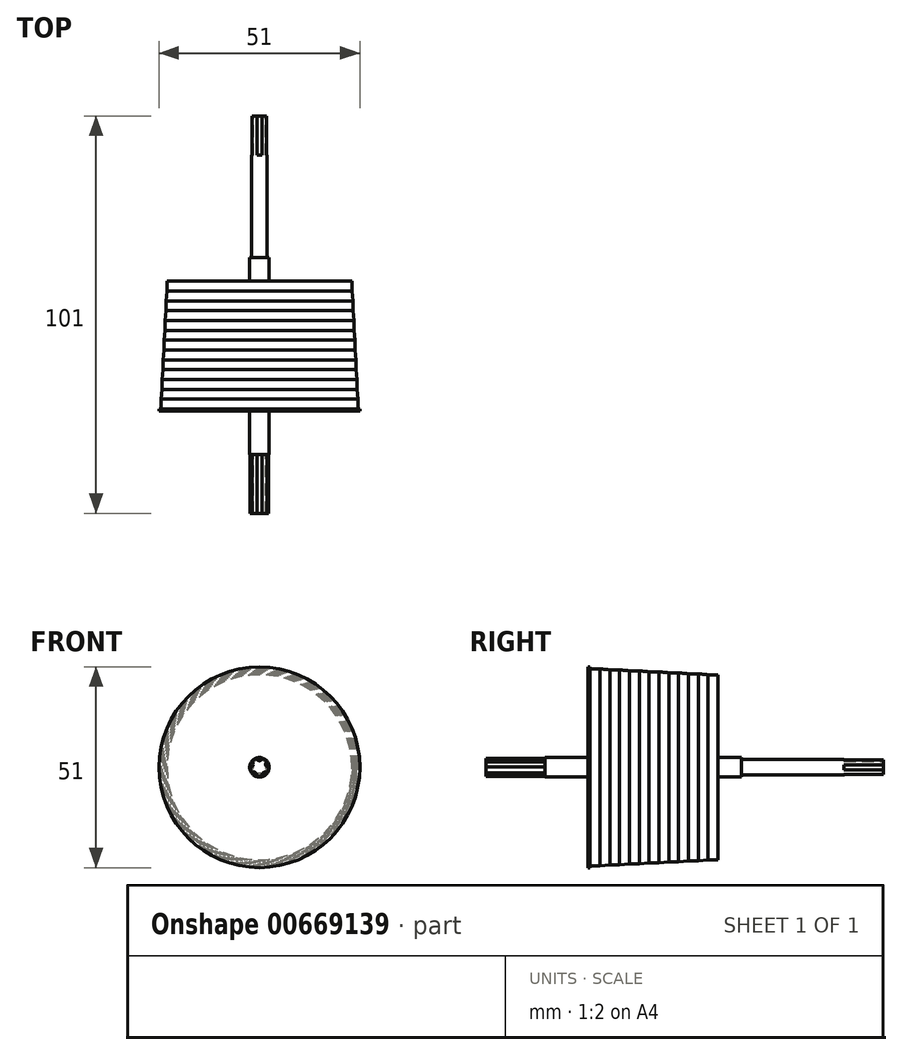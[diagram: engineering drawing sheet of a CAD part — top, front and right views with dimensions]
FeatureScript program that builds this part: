
annotation { "Feature Type Name" : "Feature", "Feature Type Description" : "" }
export const myFeature = defineFeature(function(context is Context, id is Id, definition is map)
    precondition{}
    {
        {
            var Q0;
            Q0=qCreatedBy(makeId("Front.planeOp"),FACE);
            var sketch = newSketch(context, id + "F0", { "sketchPlane" : qUnion([Q0])});
            skCircle(sketch, "E0", {"center": v(0, 0) * mm, "radius": 2.48 * mm});
            skSolve(sketch);
        }
        {
            var Q0;
            Q0 = qSketchRegion(id + "F0", true);
            extrude(context, id + "F1", {"entities" : qUnion([Q0]), "depth" : 11 * mm, "offsetDistance" : 25 * mm});
        }
        {
            var Q0;
            Q0=makeQuery(id+"F1.opExtrude","CAP_FACE",FACE,{"disambiguationData":[OSD([sQuery(id+"F0.wireOp",EDGE,"E0")])],"isStart":false});
            var sketch = newSketch(context, id + "F2", { "sketchPlane" : qUnion([Q0])});
            skCircle(sketch, "E1", {"center": v(0, 0) * mm, "radius": 2.33 * mm, "construction": true});
            skArc(sketch, "E2", {"start": v(-0.65, 2.23) * mm, "mid": v(0, 1.67) * mm, "end": v(0.65, 2.23) * mm});
            skArc(sketch, "E3.1.0", {"start": v(-2.32, 0.07) * mm, "mid": v(-1.59, 0.52) * mm, "end": v(-1.92, 1.3) * mm});
            skArc(sketch, "E3.2.0", {"start": v(-0.79, -2.19) * mm, "mid": v(-0.98, -1.35) * mm, "end": v(-1.84, -1.42) * mm});
            skArc(sketch, "E3.3.0", {"start": v(1.84, -1.42) * mm, "mid": v(0.98, -1.35) * mm, "end": v(0.79, -2.19) * mm});
            skArc(sketch, "E3.4.0", {"start": v(1.92, 1.3) * mm, "mid": v(1.59, 0.52) * mm, "end": v(2.32, 0.07) * mm});
            skArc(sketch, "E4", {"start": v(1.92, 1.3) * mm, "mid": v(1.37, 1.88) * mm, "end": v(0.65, 2.23) * mm});
            skArc(sketch, "E5.1.0", {"start": v(-0.65, 2.23) * mm, "mid": v(-1.37, 1.88) * mm, "end": v(-1.92, 1.3) * mm});
            skArc(sketch, "E5.2.0", {"start": v(-2.32, 0.07) * mm, "mid": v(-2.21, -0.72) * mm, "end": v(-1.84, -1.42) * mm});
            skArc(sketch, "E5.3.0", {"start": v(-0.79, -2.19) * mm, "mid": v(0, -2.33) * mm, "end": v(0.79, -2.19) * mm});
            skArc(sketch, "E5.4.0", {"start": v(1.84, -1.42) * mm, "mid": v(2.21, -0.72) * mm, "end": v(2.32, 0.07) * mm});
            skSolve(sketch);
        }
        {
            var Q0;
            Q0 = qSketchRegion(id + "F2", true);
            extrude(context, id + "F3", {"entities" : qUnion([Q0]), "operationType" : NewBodyOperationType.ADD, "depth" : 15 * mm, "offsetDistance" : 25 * mm});
        }
        {
            var Q0;
            Q0=qCreatedBy(makeId("Right.planeOp"),FACE);
            var sketch = newSketch(context, id + "F4", { "sketchPlane" : qUnion([Q0])});
            skLineSegment(sketch, "E6", {"start": v(0, 0) * mm, "end": v(0, 25.5) * mm});
            skLineSegment(sketch, "E7", {"start": v(0, 25.5) * mm, "end": v(0.5, 25.5) * mm});
            skLineSegment(sketch, "E8", {"start": v(0.5, 25.5) * mm, "end": v(0.5, 25) * mm});
            skLineSegment(sketch, "E9", {"start": v(0.5, 25) * mm, "end": v(3, 25) * mm});
            skLineSegment(sketch, "E10", {"start": v(3, 25) * mm, "end": v(5.5, 24.75) * mm});
            skLineSegment(sketch, "E11", {"start": v(5.5, 24.75) * mm, "end": v(8, 24.75) * mm});
            skLineSegment(sketch, "E12", {"start": v(8, 24.75) * mm, "end": v(10.5, 24.5) * mm});
            skLineSegment(sketch, "E13", {"start": v(10.5, 24.5) * mm, "end": v(13, 24.5) * mm});
            skLineSegment(sketch, "E14", {"start": v(13, 24.5) * mm, "end": v(15.5, 24.25) * mm});
            skLineSegment(sketch, "E15", {"start": v(15.5, 24.25) * mm, "end": v(18, 24.25) * mm});
            skLineSegment(sketch, "E16", {"start": v(18, 24.25) * mm, "end": v(20.5, 24) * mm});
            skLineSegment(sketch, "E17", {"start": v(20.5, 24) * mm, "end": v(23, 24) * mm});
            skLineSegment(sketch, "E18", {"start": v(23, 24) * mm, "end": v(25.5, 23.75) * mm});
            skLineSegment(sketch, "E19", {"start": v(25.5, 23.75) * mm, "end": v(28, 23.75) * mm});
            skLineSegment(sketch, "E20", {"start": v(28, 23.75) * mm, "end": v(30.5, 23.5) * mm});
            skLineSegment(sketch, "E21", {"start": v(33, 2.47) * mm, "end": v(39, 2.47) * mm});
            skLineSegment(sketch, "E22", {"start": v(75, 0) * mm, "end": v(0, 0) * mm});
            skLineSegment(sketch, "E23", {"start": v(39, 2.47) * mm, "end": v(39, 1.97) * mm});
            skLineSegment(sketch, "E24", {"start": v(39, 1.97) * mm, "end": v(75, 1.98) * mm});
            skLineSegment(sketch, "E25", {"start": v(75, 1.98) * mm, "end": v(75, 0) * mm});
            skLineSegment(sketch, "E26", {"start": v(30.5, 23.5) * mm, "end": v(33, 23.5) * mm});
            skLineSegment(sketch, "E27", {"start": v(33, 23.5) * mm, "end": v(33, 2.47) * mm});
            skSolve(sketch);
        }
        {
            var Q0;
            Q0 = qSketchRegion(id + "F4", true);
            var Q1;
            Q1=makeQuery(id+"F1.opExtrude","CAP_EDGE",EDGE,{"disambiguationData":[OSD([sQuery(id+"F0.wireOp",EDGE,"E0")])],"isStart":true});
            revolve(context, id + "F5", {"operationType" : NewBodyOperationType.ADD, "entities" : qUnion([Q0]), "axis" : qUnion([Q1]), "revolveType" : RevolveType.FULL});
        }
        {
            var Q0;
            Q0=makeQuery(id+"F5.opRevolve","SWEPT_FACE",FACE,{"disambiguationData":[OSD([sQuery(id+"F4.wireOp",EDGE,"E25")])]});
            var sketch = newSketch(context, id + "F6", { "sketchPlane" : qUnion([Q0])});
            skArc(sketch, "E28", {"start": v(-0.62, 1.87) * mm, "mid": v(0, 1.54) * mm, "end": v(0.62, 1.87) * mm});
            skArc(sketch, "E29.1.0", {"start": v(-1.87, -0.62) * mm, "mid": v(-1.54, 0) * mm, "end": v(-1.87, 0.63) * mm});
            skArc(sketch, "E29.2.0", {"start": v(0.62, -1.87) * mm, "mid": v(0, -1.54) * mm, "end": v(-0.63, -1.87) * mm});
            skArc(sketch, "E29.3.0", {"start": v(1.87, 0.62) * mm, "mid": v(1.54, 0) * mm, "end": v(1.87, -0.63) * mm});
            skPoint(sketch, "E29.center", {"position": v(0, 0) * mm});
            skArc(sketch, "E30", {"start": v(-1.87, 0.62) * mm, "mid": v(-1.97, 0) * mm, "end": v(-1.87, -0.63) * mm});
            skArc(sketch, "E31.1.0", {"start": v(-0.62, -1.87) * mm, "mid": v(0, -1.97) * mm, "end": v(0.63, -1.87) * mm});
            skArc(sketch, "E31.2.0", {"start": v(1.87, -0.62) * mm, "mid": v(1.97, 0) * mm, "end": v(1.87, 0.63) * mm});
            skArc(sketch, "E31.3.0", {"start": v(0.62, 1.87) * mm, "mid": v(0, 1.97) * mm, "end": v(-0.63, 1.87) * mm});
            skSolve(sketch);
        }
        {
            var Q0;
            Q0 = qSketchRegion(id + "F6", true);
            extrude(context, id + "F7", {"entities" : qUnion([Q0]), "operationType" : NewBodyOperationType.REMOVE, "oppositeDirection" : true, "depth" : 10 * mm, "offsetDistance" : 25 * mm});
        }
    });
